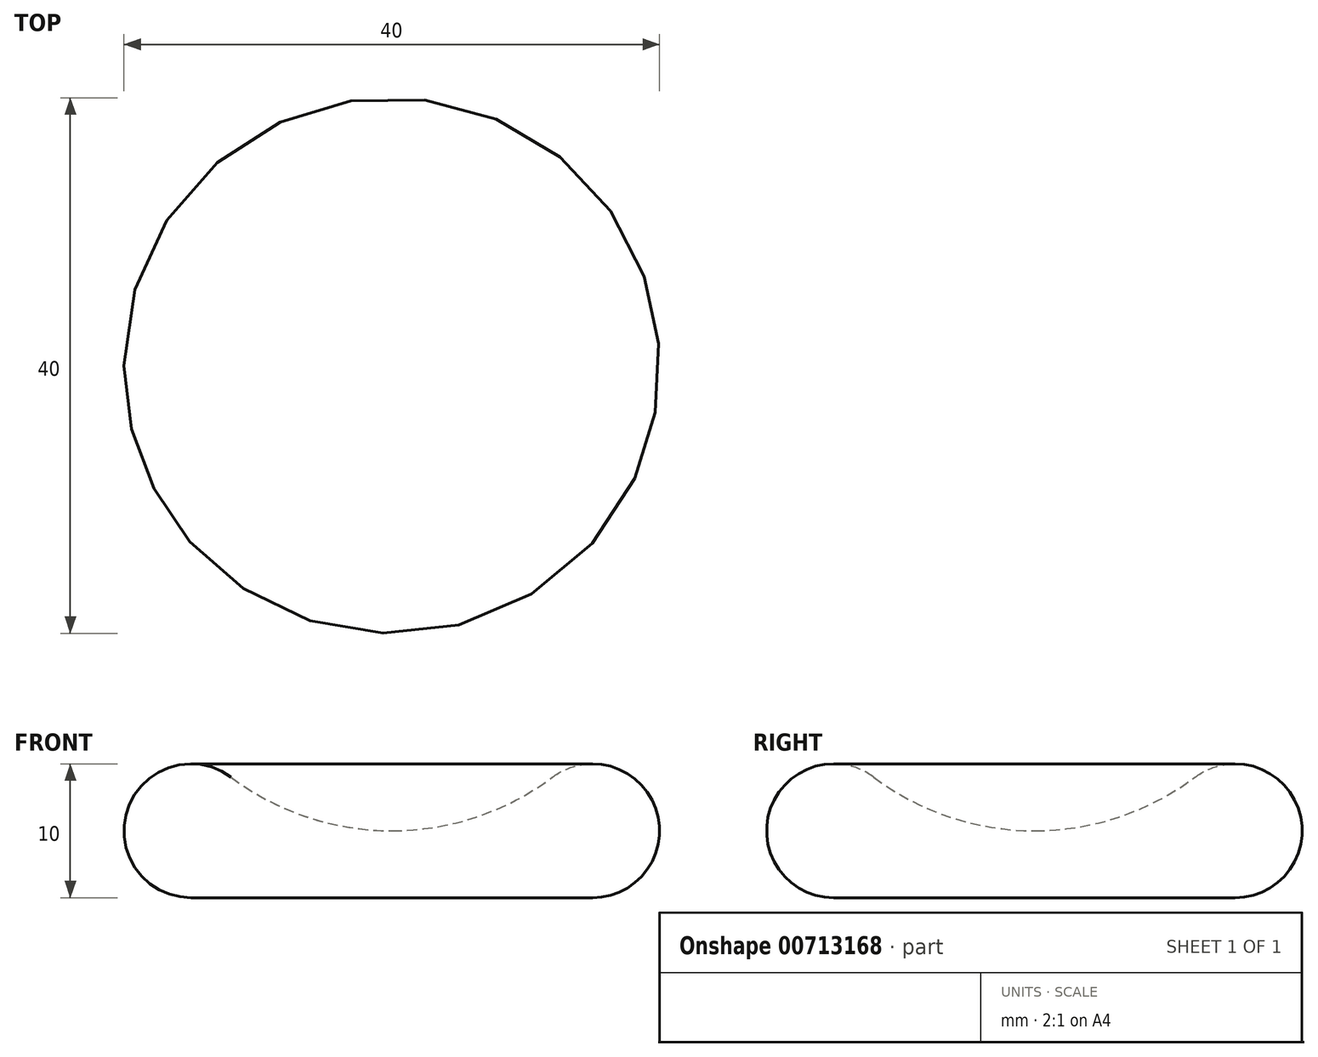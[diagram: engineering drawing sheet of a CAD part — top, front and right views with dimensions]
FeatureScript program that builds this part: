
annotation { "Feature Type Name" : "Feature", "Feature Type Description" : "" }
export const myFeature = defineFeature(function(context is Context, id is Id, definition is map)
    precondition{}
    {
        {
            var Q0;
            Q0=qCreatedBy(makeId("Front.planeOp"),FACE);
            var sketch = newSketch(context, id + "F0", { "sketchPlane" : qUnion([Q0])});
            skArc(sketch, "E0", {"start": v(-12, 9) * mm, "mid": v(-19.74, 6.58) * mm, "end": v(-15, 0) * mm});
            skArc(sketch, "E1", {"start": v(-12, 9) * mm, "mid": v(-6.32, 6.03) * mm, "end": v(0, 5) * mm});
            skLineSegment(sketch, "E2", {"start": v(0, 0) * mm, "end": v(-15, 0) * mm});
            skLineSegment(sketch, "E3", {"start": v(0, 0) * mm, "end": v(0, 5) * mm});
            skSolve(sketch);
        }
        {
            var Q0;
            Q0=makeQuery(id+"F0.imprint","IMPRINT",FACE,{"disambiguationData":[TD([[makeQuery(id+"F0.imprint","IMPRINT",EDGE,{"derivedFrom":sQuery(id+"F0.wireOp",EDGE,"E0")}),1.0]])]});
            var Q1;
            Q1=sQuery(id+"F0.wireOp",EDGE,"E3");
            revolve(context, id + "F1", {"surfaceOperationType" : NewSurfaceOperationType.NEW, "entities" : qUnion([Q0]), "axis" : qUnion([Q1]), "revolveType" : RevolveType.FULL});
        }
    });
